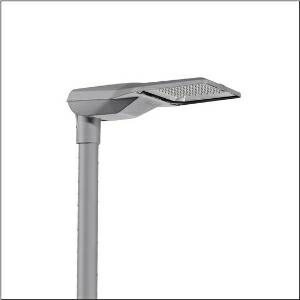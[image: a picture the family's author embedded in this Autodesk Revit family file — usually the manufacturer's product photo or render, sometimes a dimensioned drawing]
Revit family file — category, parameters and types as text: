
# Revit family: streetlight_sl_21_iq_midi___st1_5a_5xe3p41g08mb_0a3d
name_source: partatom
category: Lighting Fixtures
units: mm (PartAtom-declared; Revit-internal decimal feet)

## family parameters
Cut with Voids When Loaded = No
Host = Face
Light Source = No
Part Type = Normal
Room Calculation Point = No
Round Connector Dimension = Use Diameter
Shared = No

## types (1)
- --- (1 x LED, 20000 lm, 146.7 W, 4000K)
    Apparent Load = 147 VA
    CIE Flux Codes = 22 53 95 100 100
    Color Rendering = 70
    Color Temperature = 4000K
    Default Elevation = 1800 mm
    Description = Streetlight SL 21 iQ midi, mast luminaire, primary light control with lens, of PMMA, primary optical cover: cover, of toughened safety glass, transparent, light distribution: ST1.5a, light emission: direct distribution, primary light characteristic: asymmetric, installation type: post-top, side-entry, LED, High Power LED, rated luminous flux: 20.000lm, luminous efficacy: 136lm/W, light colour: 740, colour temperature: 4000K, control gear: iQ Street-Remote, control: Street-Remote, Auto-Match, Temp-Guard, Lumen-Switch, Night-Set, Smart-Wire, Light-Fading, Desk-Remote (wireless, voltage-free reading and setting of iQ features in the workshop via application-optimized NFC function/RFID function), optimised constant luminous flux control (CLO 2.0), pre-setting: linear dimming characteristic, mains connection: 230..240V, AC, 50/60Hz, start of lifetime: 147W, end of service life: 161W, reduction: 62W, luminaire housing, of diecast aluminium, powder-coated, SITECO metallic grey (DB 702S), corrosivity category C5 high according to DIN EN ISO 12944, please order mast flange separately, inclination adjustable: 0°, 5°, 10°, 15°, sealing non-destructively replaceable, multi-level sealing system, length: 644mm, width: 335mm, height: 110mm, mast flange for spigot size: 42mm (side-entry): 5XC10008XM4, 60/48mm (side-entry/post-top): 5XC10108XM2, 76/60mm (side-entry/post-top): 5XC10108XM1, mounting height: 4..8m, protection rating (complete): IP66, insulation class (complete): insulation class II (safety insulation), certification: CE, ENEC, ENEC+, VDE, impact resistance: IK10, permissible operating ambient temperature for outdoor applications: -40..+50°C, standard-compliant lighting for roads and squares, packaging unit: 1 piece

Light Distribution: ST1.5a
    Height = 111 mm
    Lamp = 1 x LED
    Lamp Light Flux = 20000 lm
    Lamp Power = 146.7 W
    Lamp count = 1
    Length = 644 mm
    Luminous efficacy = 136 lm/W
    Manufacturer = Siteco
    ModVariant = No
    Model = 5XE3P41G08MB
    Number of Poles = 1
    OnlyDefault = Yes
    Power Factor = 1
    Product Name = Streetlight SL 21 iQ midi | ST1.5a
    Product group = mast luminaire | pylon top
    ProductGroupID = 6100
    Protection Class = Protection class II
    Protection Degree = IP 66
    RLX_Detail_Level = 1
    RLX_Emergency_Light_Flux = 0 lm
    RLX_Emergency_Type = 0
    RLX_Emergency_Type_DB = No
    RlxData = <blob elided: 30457 chars, md5=7fd509c4>
    Socket = socket
    Standby Power = 0 W
    System Light Flux = 20000 lm
    System Power = 147 W
    Type Comments = factory setting: luminous flux: 100 % | dim-lin: 254 | 753 mA
    Type Image = l_1004298.jpg
    URL = http://relux.com
    VarID = @adj_175697
    Voltage = 0 V
    Weight = 0.00 kg
    Width = 336 mm

## geometry (parser evidence)
native form markers: Blend x4, Sweep x12
no freeform markers — native parametric forms only
